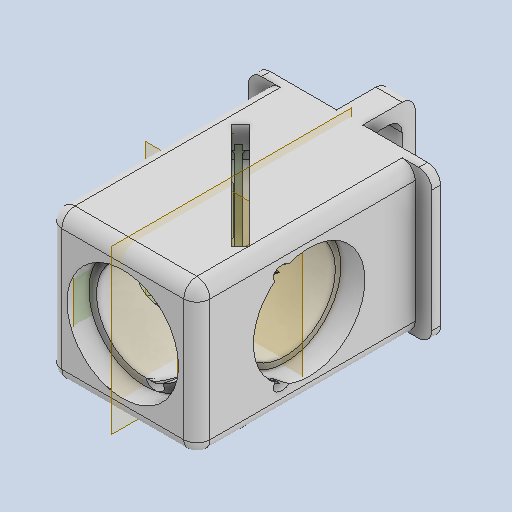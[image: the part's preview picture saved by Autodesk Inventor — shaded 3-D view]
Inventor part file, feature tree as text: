
AUTODESK INVENTOR PART (.ipt)
format: ipt  version: 2023 (Build 270158000, 158)  size: 468,480 bytes
history: native  units: in
note: dims shown in document units (in); Inventor stores cm internally (conversion verified against a paired STEP export)
features: extrude x11, sketch x11, projected_geometry x6, other x5, plane x4, reference x2, fillet x1
ambient origin geometry x8: Origin, YZ Plane, XZ Plane, XY Plane, X Axis, Y Axis, Z Axis, Center Point
bodies: Solid1 (feature_tree)
feature tree (40):
  plane  "Work Plane1"
  extrude  "Extrusion1"  Depth=1.3346in
  extrude  "Extrusion2"  Depth=1.0039in
  extrude  "Extrusion3"  Depth=0.9055in
  extrude  "Extrusion4"  Depth=1.0039in
  extrude  "Extrusion5"  Depth=0.8661in
  extrude  "Extrusion6"  Depth=1.6535in
  extrude  "Extrusion7"  Depth=0.0512in
  extrude  "Extrusion8"  Depth=1.3386in
  plane  "Work Plane2"
  extrude  "Extrusion9"  Depth=0.1181in
  fillet  "Fillet1"  Radius=1.2992in
  extrude  "Extrusion10"  Depth=0.8661in
  plane  "Work Plane3"
  extrude  "Extrusion11"  Depth=0.1181in
  plane  "Work Plane4"
  sketch  "Sketch1"  dims[d0=1.3346in d1=1.3346in]
  reference  "Reference1"
  reference  "Reference2"
  sketch  "Sketch2"  dims[d2=1.9685in d3=0.0in d4=1.0039in]
  projected_geometry  "Projected Loop1"
  sketch  "Sketch3"  dims[d5=0.2165in d6=0.0in d7=0.9055in]
  sketch  "Sketch4"  dims[d8=0.0in d9=0.0in d10=1.0039in]
  projected_geometry  "Projected Loop2"
  sketch  "Sketch5"  dims[d11=0.1969in d12=0.0in d13=0.8661in]
  sketch  "Sketch6"  dims[d14=0.1969in d15=0.0in d16=1.6535in]
  sketch  "Sketch7"  dims[d17=45.0deg d18=0.0512in]
  projected_geometry  "Projected Loop3"
  sketch  "Sketch8"  dims[d19=1.1811in d20=0.0in d21=1.3386in]
  sketch  "Sketch9"  dims[d22=135.0deg d23=0.1181in d24=1.2992in d25=0.0in]
  projected_geometry  "Projected Loop4"
  sketch  "Sketch10"  dims[d26=1.3386in d27=0.8661in]
  projected_geometry  "Projected Loop5"
  projected_geometry  "Projected Loop6"
  sketch  "Sketch11"  dims[d28=0.1142in d29=0.1142in d30=0.1142in d31=0.1142in d32=1.1811in d33=0.0in d34=-0.6693in d35=0.5512in d36=0.1181in d37=0.2362in d38=0.0in d39=0.1181in d40=1.6535in d41=0.1181in d42=0.0787in d43=0.0in d44=-0.2008in d45=0.9961in d46=0.1181in d47=0.0in d50=0.0866in d51=-0.1969in]
  other  "<userpath>\Dropbox\UC2\02_CAD\INVENTOR\uc2_v3\Assembly_Cube_Beamsplitter_new_v3.iam"
  other  "Assembly_Cube_Beamsplitter_new_v3.iam"
  other  "10_Cube_1x1_IM:2"
  other  "10_Cube_1x1_IM:1"
  other  "30_Cube_Insert_Filter_Revolver_Filter_base_single:1"
